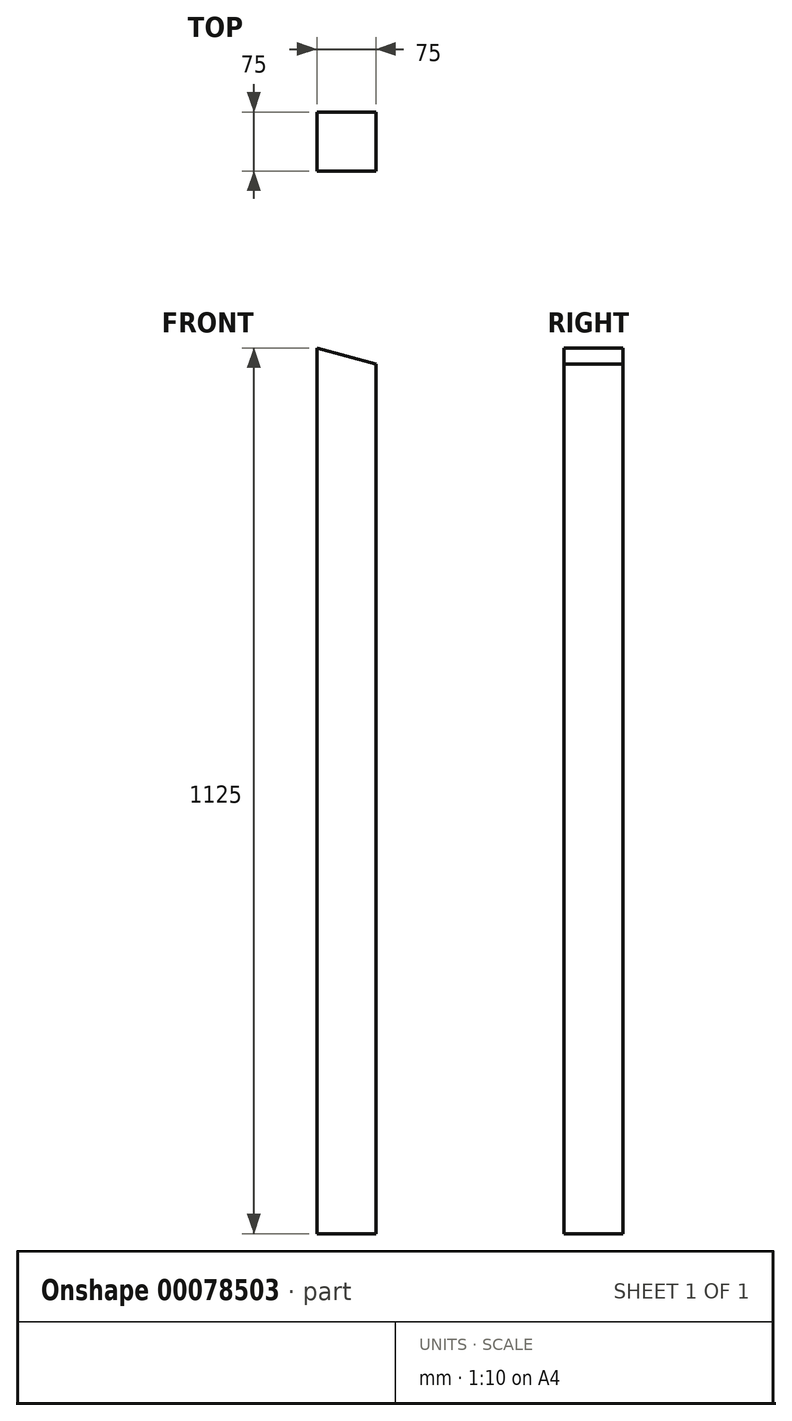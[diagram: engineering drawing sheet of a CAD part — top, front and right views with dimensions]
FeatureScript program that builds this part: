
annotation { "Feature Type Name" : "Feature", "Feature Type Description" : "" }
export const myFeature = defineFeature(function(context is Context, id is Id, definition is map)
    precondition{}
    {
        {
            var Q0;
            Q0=qCreatedBy(makeId("Top.planeOp"),FACE);
            var sketch = newSketch(context, id + "F0", { "sketchPlane" : qUnion([Q0])});
            skLineSegment(sketch, "E0.bottom", {"start": v(37.5, -37.5) * mm, "end": v(-37.5, -37.5) * mm});
            skLineSegment(sketch, "E0.top", {"start": v(37.5, 37.5) * mm, "end": v(-37.5, 37.5) * mm});
            skLineSegment(sketch, "E0.left", {"start": v(37.5, -37.5) * mm, "end": v(37.5, 37.5) * mm});
            skLineSegment(sketch, "E0.right", {"start": v(-37.5, -37.5) * mm, "end": v(-37.5, 37.5) * mm});
            skPoint(sketch, "E0.middle", {"position": v(0, 0) * mm});
            skSolve(sketch);
        }
        {
            var Q0;
            Q0=makeQuery(id+"F0.imprint","IMPRINT",FACE,{"disambiguationData":[TD([[makeQuery(id+"F0.imprint","IMPRINT",EDGE,{"derivedFrom":sQuery(id+"F0.wireOp",EDGE,"E0.bottom")}),-1.0]])]});
            extrude(context, id + "F1", {"entities" : qUnion([Q0]), "depth" : 1125 * mm});
        }
        {
            var Q0;
            Q0=makeQuery(id+"F1.opExtrude","CAP_EDGE",EDGE,{"disambiguationData":[OSD([sQuery(id+"F0.wireOp",EDGE,"E0.left")])],"isStart":false});
            chamfer(context, id + "F2", {"entities" : qUnion([Q0]), "chamferType" : ChamferType.OFFSET_ANGLE, "width" : 75 * mm, "oppositeDirection" : false, "angle" : 15 * degree, "tangentPropagation" : true});
        }
    });
